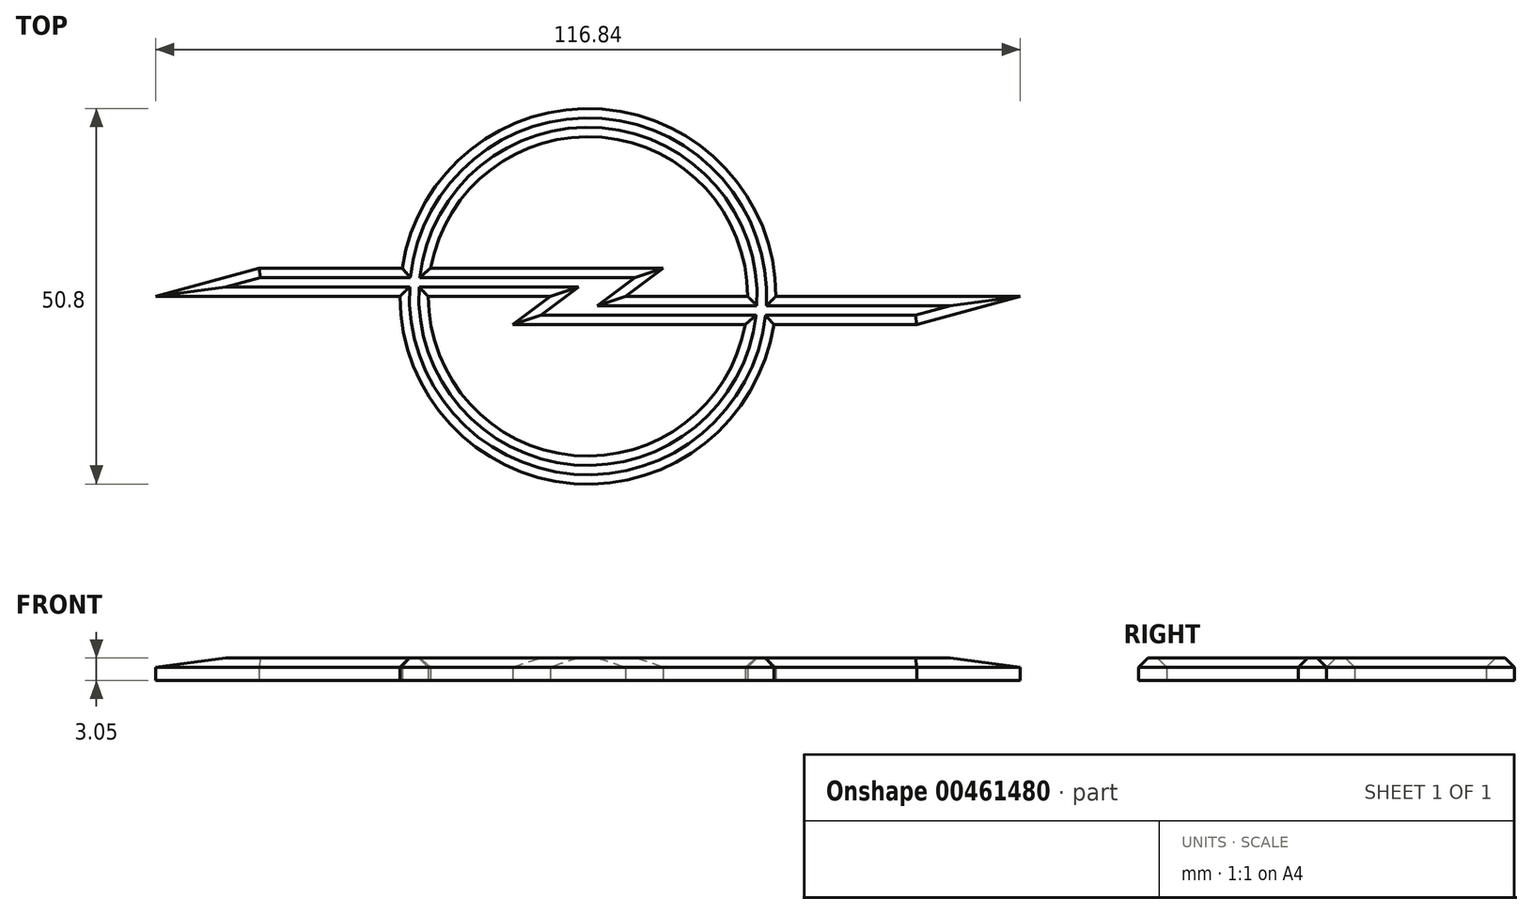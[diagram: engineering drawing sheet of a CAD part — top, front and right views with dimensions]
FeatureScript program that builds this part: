
annotation { "Feature Type Name" : "Feature", "Feature Type Description" : "" }
export const myFeature = defineFeature(function(context is Context, id is Id, definition is map)
    precondition{}
    {
        {
            var Q0;
            Q0=qCreatedBy(makeId("Top.planeOp"),FACE);
            var sketch = newSketch(context, id + "F0", { "sketchPlane" : qUnion([Q0])});
            skLineSegment(sketch, "E0", {"start": v(-44.45, 3.81) * mm, "end": v(-25.11, 3.81) * mm});
            skLineSegment(sketch, "E1", {"start": v(10.16, 3.81) * mm, "end": v(5.08, 0) * mm});
            skLineSegment(sketch, "E2", {"start": v(5.08, 0) * mm, "end": v(21.59, 0) * mm});
            skLineSegment(sketch, "E3", {"start": v(58.42, 0) * mm, "end": v(44.45, -3.8) * mm});
            skLineSegment(sketch, "E4", {"start": v(44.45, -3.8) * mm, "end": v(25.11, -3.8) * mm});
            skLineSegment(sketch, "E5", {"start": v(-10.16, -3.81) * mm, "end": v(-5.08, 0) * mm});
            skLineSegment(sketch, "E6", {"start": v(-5.08, 0) * mm, "end": v(-21.59, 0) * mm});
            skLineSegment(sketch, "E7", {"start": v(-58.42, 0) * mm, "end": v(-44.45, 3.81) * mm});
            skLineSegment(sketch, "E8", {"start": v(-21.25, 3.81) * mm, "end": v(10.16, 3.81) * mm});
            skLineSegment(sketch, "E9", {"start": v(-25.4, 0) * mm, "end": v(-58.42, 0) * mm});
            skArc(sketch, "E10", {"start": v(-21.59, 0) * mm, "mid": v(-1.91, -21.5) * mm, "end": v(21.25, -3.8) * mm});
            skArc(sketch, "E11", {"start": v(-25.4, 0) * mm, "mid": v(-1.91, -25.33) * mm, "end": v(25.11, -3.8) * mm});
            skLineSegment(sketch, "E12", {"start": v(25.4, 0) * mm, "end": v(58.42, 0) * mm});
            skLineSegment(sketch, "E13", {"start": v(21.25, -3.8) * mm, "end": v(-10.16, -3.81) * mm});
            skArc(sketch, "E14", {"start": v(21.59, 0) * mm, "mid": v(1.91, 21.5) * mm, "end": v(-21.25, 3.8) * mm});
            skArc(sketch, "E15", {"start": v(25.4, 0) * mm, "mid": v(1.91, 25.33) * mm, "end": v(-25.11, 3.81) * mm});
            skSolve(sketch);
        }
        {
            var Q0;
            Q0=makeQuery(id+"F0.imprint","IMPRINT",FACE,{"disambiguationData":[TD([[makeQuery(id+"F0.imprint","IMPRINT",EDGE,{"derivedFrom":sQuery(id+"F0.wireOp",EDGE,"E0")}),-1.0]])]});
            extrude(context, id + "F1", {"entities" : qUnion([Q0]), "depth" : 3.05 * mm});
        }
        {
            var Q0;
            Q0=makeQuery(id+"F1.opExtrude","CAP_EDGE",EDGE,{"disambiguationData":[OSD([sQuery(id+"F0.wireOp",EDGE,"E7")])],"isStart":false});
            var Q1;
            Q1=makeQuery(id+"F1.opExtrude","CAP_EDGE",EDGE,{"disambiguationData":[OSD([sQuery(id+"F0.wireOp",EDGE,"E0")])],"isStart":false});
            var Q2;
            Q2=makeQuery(id+"F1.opExtrude","CAP_EDGE",EDGE,{"disambiguationData":[OSD([sQuery(id+"F0.wireOp",EDGE,"E9")])],"isStart":false});
            var Q3;
            Q3=makeQuery(id+"F1.opExtrude","CAP_EDGE",EDGE,{"disambiguationData":[OSD([sQuery(id+"F0.wireOp",EDGE,"E11")])],"isStart":false});
            var Q4;
            Q4=makeQuery(id+"F1.opExtrude","CAP_EDGE",EDGE,{"disambiguationData":[OSD([sQuery(id+"F0.wireOp",EDGE,"E10")])],"isStart":false});
            var Q5;
            Q5=makeQuery(id+"F1.opExtrude","CAP_EDGE",EDGE,{"disambiguationData":[OSD([sQuery(id+"F0.wireOp",EDGE,"E13")])],"isStart":false});
            var Q6;
            Q6=makeQuery(id+"F1.opExtrude","CAP_EDGE",EDGE,{"disambiguationData":[OSD([sQuery(id+"F0.wireOp",EDGE,"E2")])],"isStart":false});
            var Q7;
            Q7=makeQuery(id+"F1.opExtrude","CAP_EDGE",EDGE,{"disambiguationData":[OSD([sQuery(id+"F0.wireOp",EDGE,"E1")])],"isStart":false});
            var Q8;
            Q8=makeQuery(id+"F1.opExtrude","CAP_EDGE",EDGE,{"disambiguationData":[OSD([sQuery(id+"F0.wireOp",EDGE,"E8")])],"isStart":false});
            var Q9;
            Q9=makeQuery(id+"F1.opExtrude","CAP_EDGE",EDGE,{"disambiguationData":[OSD([sQuery(id+"F0.wireOp",EDGE,"E6")])],"isStart":false});
            var Q10;
            Q10=makeQuery(id+"F1.opExtrude","CAP_EDGE",EDGE,{"disambiguationData":[OSD([sQuery(id+"F0.wireOp",EDGE,"E5")])],"isStart":false});
            var Q11;
            Q11=makeQuery(id+"F1.opExtrude","CAP_EDGE",EDGE,{"disambiguationData":[OSD([sQuery(id+"F0.wireOp",EDGE,"E14")])],"isStart":false});
            var Q12;
            Q12=makeQuery(id+"F1.opExtrude","CAP_EDGE",EDGE,{"disambiguationData":[OSD([sQuery(id+"F0.wireOp",EDGE,"E15")])],"isStart":false});
            var Q13;
            Q13=makeQuery(id+"F1.opExtrude","CAP_EDGE",EDGE,{"disambiguationData":[OSD([sQuery(id+"F0.wireOp",EDGE,"E12")])],"isStart":false});
            var Q14;
            Q14=makeQuery(id+"F1.opExtrude","CAP_EDGE",EDGE,{"disambiguationData":[OSD([sQuery(id+"F0.wireOp",EDGE,"E4")])],"isStart":false});
            var Q15;
            Q15=makeQuery(id+"F1.opExtrude","CAP_EDGE",EDGE,{"disambiguationData":[OSD([sQuery(id+"F0.wireOp",EDGE,"E3")])],"isStart":false});
            chamfer(context, id + "F2", {"entities" : qUnion([Q0, Q1, Q2, Q3, Q4, Q5, Q6, Q7, Q8, Q9, Q10, Q11, Q12, Q13, Q14, Q15]), "width" : 1.27 * mm, "tangentPropagation" : true});
        }
    });
